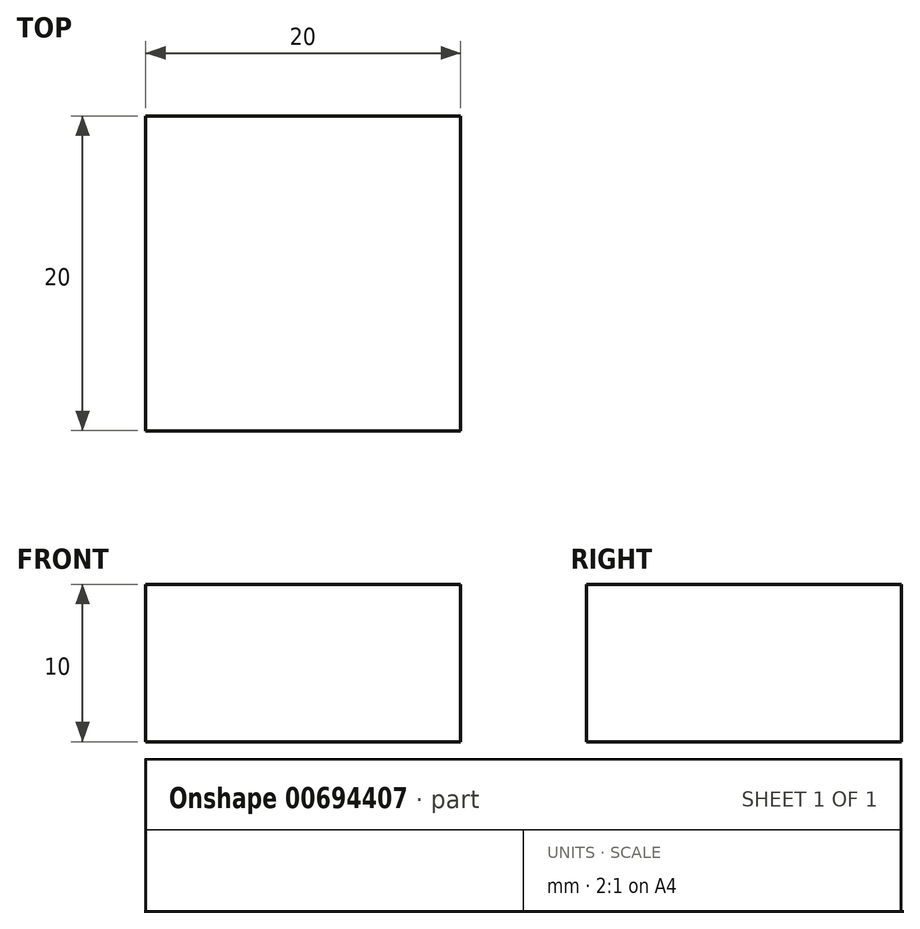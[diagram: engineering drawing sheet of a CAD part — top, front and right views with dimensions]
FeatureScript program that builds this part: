
annotation { "Feature Type Name" : "Feature", "Feature Type Description" : "" }
export const myFeature = defineFeature(function(context is Context, id is Id, definition is map)
    precondition{}
    {
        {
            var Q0;
            Q0=qCreatedBy(makeId("Top.planeOp"),FACE);
            var sketch = newSketch(context, id + "F0", { "sketchPlane" : qUnion([Q0])});
            skLineSegment(sketch, "E0.bottom", {"start": v(-10.27, 9.85) * mm, "end": v(9.73, 9.85) * mm});
            skLineSegment(sketch, "E0.top", {"start": v(-10.27, -10.15) * mm, "end": v(9.73, -10.15) * mm});
            skLineSegment(sketch, "E0.left", {"start": v(-10.27, 9.85) * mm, "end": v(-10.27, -10.15) * mm});
            skLineSegment(sketch, "E0.right", {"start": v(9.73, 9.85) * mm, "end": v(9.73, -10.15) * mm});
            skSolve(sketch);
        }
        {
            var Q0;
            Q0 = qSketchRegion(id + "F0", true);
            extrude(context, id + "F1", {"entities" : qUnion([Q0]), "depth" : 10 * mm, "offsetDistance" : 25 * mm});
        }
    });
